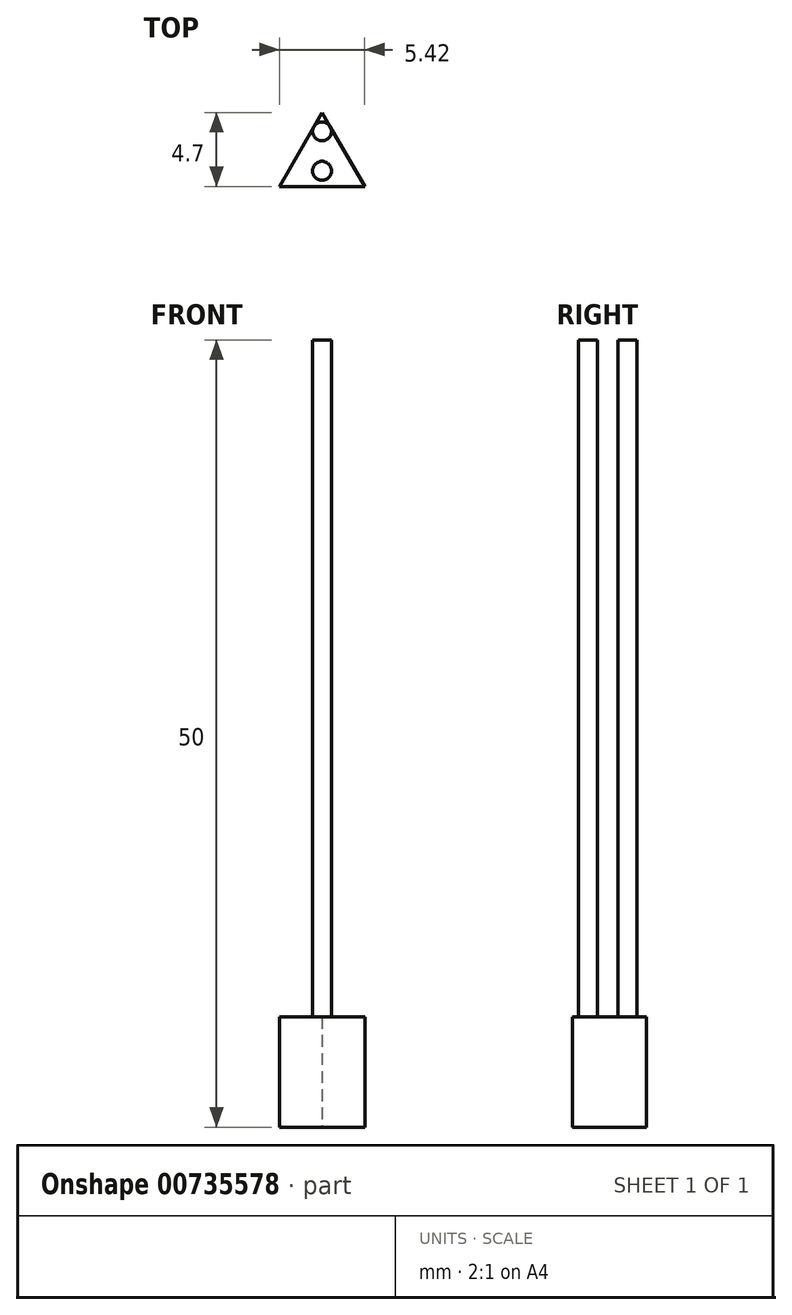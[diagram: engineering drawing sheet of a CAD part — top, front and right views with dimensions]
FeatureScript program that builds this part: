
annotation { "Feature Type Name" : "Feature", "Feature Type Description" : "" }
export const myFeature = defineFeature(function(context is Context, id is Id, definition is map)
    precondition{}
    {
        {
            var Q0;
            Q0=qCreatedBy(makeId("Top.planeOp"),FACE);
            var sketch = newSketch(context, id + "F0", { "sketchPlane" : qUnion([Q0])});
            skLineSegment(sketch, "E0", {"start": v(-2.71, -4.7) * mm, "end": v(2.71, -4.7) * mm});
            skLineSegment(sketch, "E1", {"start": v(2.71, -4.7) * mm, "end": v(0, 0) * mm});
            skLineSegment(sketch, "E2", {"start": v(0, 0) * mm, "end": v(-2.71, -4.7) * mm});
            skLineSegment(sketch, "E3", {"start": v(0, 0) * mm, "end": v(0, -4.7) * mm, "construction": true});
            skCircle(sketch, "E4", {"center": v(0, -3.7) * mm, "radius": 0.6 * mm});
            skCircle(sketch, "E5", {"center": v(0, -1.2) * mm, "radius": 0.6 * mm});
            skSolve(sketch);
        }
        {
            var Q0;
            Q0=makeQuery(id+"F0.imprint","IMPRINT",FACE,{"disambiguationData":[TD([[makeQuery(id+"F0.imprint","IMPRINT",EDGE,{"derivedFrom":sQuery(id+"F0.wireOp",EDGE,"E0")}),1.0]])]});
            var Q1;
            {var subQ0=sQuery(id+"F0.wireOp",EDGE,"E2");var subQ1=sQuery(id+"F0.wireOp",EDGE,"E1");var subQ2=makeQuery(id+"F0.imprint","INTERSECT",VERTEX,{"derivedFrom":[subQ1,subQ0]});Q1=makeQuery(id+"F0.imprint","IMPRINT",FACE,{"disambiguationData":[TD([[makeQuery(id+"F0.imprint","IMPRINT",EDGE,{"disambiguationData":[TD([[subQ2,1.0]])],"derivedFrom":subQ1}),1.0]])]});}
            var Q2;
            {var subQ0=sQuery(id+"F0.wireOp",EDGE,"E5");var subQ1=makeQuery(id+"F0.imprint","INTERSECT",VERTEX,{"derivedFrom":[sQuery(id+"F0.wireOp",EDGE,"E1"),subQ0]});Q2=makeQuery(id+"F0.imprint","IMPRINT",FACE,{"disambiguationData":[TD([[makeQuery(id+"F0.imprint","IMPRINT",EDGE,{"disambiguationData":[TD([[subQ1,-1.0]])],"derivedFrom":subQ0}),1.0]])]});}
            var Q3;
            Q3=makeQuery(id+"F0.imprint","IMPRINT",FACE,{"disambiguationData":[TD([[makeQuery(id+"F0.imprint","IMPRINT",EDGE,{"derivedFrom":sQuery(id+"F0.wireOp",EDGE,"E4")}),1.0]])]});
            extrude(context, id + "F1", {"entities" : qUnion([Q0, Q1, Q2, Q3]), "depth" : 7 * mm, "offsetDistance" : 25 * mm});
        }
        {
            var Q0;
            {var subQ0=sQuery(id+"F0.wireOp",EDGE,"E5");var subQ1=makeQuery(id+"F0.imprint","INTERSECT",VERTEX,{"derivedFrom":[sQuery(id+"F0.wireOp",EDGE,"E1"),subQ0]});Q0=makeQuery(id+"F0.imprint","IMPRINT",FACE,{"disambiguationData":[TD([[makeQuery(id+"F0.imprint","IMPRINT",EDGE,{"disambiguationData":[TD([[subQ1,-1.0]])],"derivedFrom":subQ0}),1.0]])]});}
            var Q1;
            Q1=makeQuery(id+"F0.imprint","IMPRINT",FACE,{"disambiguationData":[TD([[makeQuery(id+"F0.imprint","IMPRINT",EDGE,{"derivedFrom":sQuery(id+"F0.wireOp",EDGE,"E4")}),1.0]])]});
            extrude(context, id + "F2", {"entities" : qUnion([Q0, Q1]), "operationType" : NewBodyOperationType.ADD, "depth" : 50 * mm, "offsetDistance" : 25 * mm});
        }
    });
